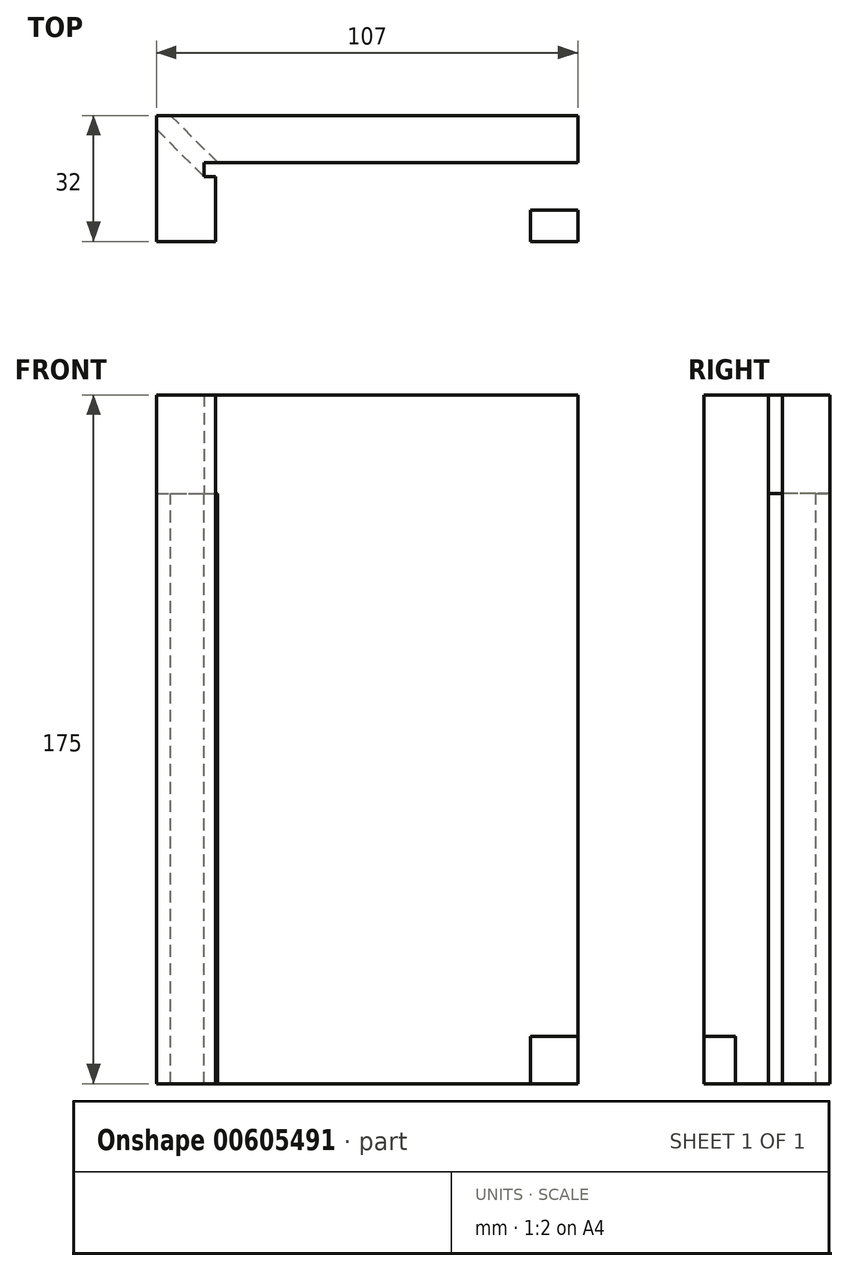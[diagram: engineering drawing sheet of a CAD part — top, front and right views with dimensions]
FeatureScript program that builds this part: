
annotation { "Feature Type Name" : "Feature", "Feature Type Description" : "" }
export const myFeature = defineFeature(function(context is Context, id is Id, definition is map)
    precondition{}
    {
        {
            var Q0;
            Q0=qCreatedBy(makeId("Top.planeOp"),FACE);
            var sketch = newSketch(context, id + "F0", { "sketchPlane" : qUnion([Q0])});
            skLineSegment(sketch, "E0", {"start": v(-28.32, 70.71) * mm, "end": v(-28.32, -10.33) * mm, "construction": true});
            skLineSegment(sketch, "E1", {"start": v(-27.64, -6.28) * mm, "end": v(-11.03, -22.9) * mm, "construction": true});
            skLineSegment(sketch, "E2", {"start": v(-15.41, -17.56) * mm, "end": v(106.8, -17.56) * mm, "construction": true});
            skLineSegment(sketch, "E3.0", {"start": v(-26.02, 70.71) * mm, "end": v(-26.02, -10.33) * mm, "construction": true});
            skLineSegment(sketch, "E4.0", {"start": v(-26.02, -4.66) * mm, "end": v(-9.4, -21.27) * mm, "construction": true});
            skLineSegment(sketch, "E5.0", {"start": v(-15.41, -15.26) * mm, "end": v(106.8, -15.26) * mm, "construction": true});
            skLineSegment(sketch, "E6.bottom", {"start": v(-15.41, -15.26) * mm, "end": v(79.59, -15.26) * mm});
            skLineSegment(sketch, "E6.top", {"start": v(-15.41, -3.26) * mm, "end": v(79.59, -3.26) * mm});
            skLineSegment(sketch, "E6.left", {"start": v(-15.41, -15.26) * mm, "end": v(-15.41, -3.26) * mm});
            skLineSegment(sketch, "E6.right", {"start": v(79.59, -15.26) * mm, "end": v(79.59, -3.26) * mm});
            skLineSegment(sketch, "E7.bottom", {"start": v(-15.41, -15.26) * mm, "end": v(-27.41, -15.26) * mm});
            skLineSegment(sketch, "E7.top", {"start": v(-15.41, -35.26) * mm, "end": v(-27.41, -35.26) * mm});
            skLineSegment(sketch, "E7.left", {"start": v(-15.41, -15.26) * mm, "end": v(-15.41, -35.26) * mm});
            skLineSegment(sketch, "E7.right", {"start": v(-27.41, -15.26) * mm, "end": v(-27.41, -35.26) * mm});
            skLineSegment(sketch, "E8.top", {"start": v(-15.41, -3.26) * mm, "end": v(-27.41, -3.26) * mm});
            skLineSegment(sketch, "E8.right", {"start": v(-27.41, -15.26) * mm, "end": v(-27.41, -3.26) * mm});
            skLineSegment(sketch, "E9", {"start": v(-27.41, -3.26) * mm, "end": v(-15.41, -15.26) * mm});
            skLineSegment(sketch, "E10.0", {"start": v(-27.79, -6.42) * mm, "end": v(-11.17, -23.04) * mm});
            skLineSegment(sketch, "E11.0", {"start": v(-23.88, -3.26) * mm, "end": v(-7.64, -19.5) * mm});
            skSolve(sketch);
        }
        {
            var Q0;
            {var subQ1=sQuery(id+"F0.wireOp",EDGE,"E6.top");Q0=makeQuery(id+"F0.imprint","IMPRINT",FACE,{"disambiguationData":[TD([[makeQuery(id+"F0.imprint","IMPRINT",EDGE,{"derivedFrom":subQ1}),-1.0]])]});}
            var Q1;
            {var subQ1=sQuery(id+"F0.wireOp",EDGE,"E8.top");var subQ3=sQuery(id+"F0.wireOp",EDGE,"E11.0");var subQ4=makeQuery(id+"F0.imprint","INTERSECT",VERTEX,{"derivedFrom":[subQ1,subQ3]});Q1=makeQuery(id+"F0.imprint","IMPRINT",FACE,{"disambiguationData":[TD([[makeQuery(id+"F0.imprint","IMPRINT",EDGE,{"disambiguationData":[TD([[subQ4,-1.0]])],"derivedFrom":subQ3}),1.0]])]});}
            var Q2;
            {var subQ0=sQuery(id+"F0.wireOp",EDGE,"E9");Q2=makeQuery(id+"F0.imprint","IMPRINT",FACE,{"disambiguationData":[TD([[makeQuery(id+"F0.imprint","IMPRINT",EDGE,{"derivedFrom":subQ0}),-1.0]])]});}
            var Q3;
            {var subQ0=sQuery(id+"F0.wireOp",EDGE,"E8.right");var subQ3=sQuery(id+"F0.wireOp",EDGE,"E10.0");var subQ5=makeQuery(id+"F0.imprint","INTERSECT",VERTEX,{"derivedFrom":[subQ0,subQ3]});Q3=makeQuery(id+"F0.imprint","IMPRINT",FACE,{"disambiguationData":[TD([[makeQuery(id+"F0.imprint","IMPRINT",EDGE,{"disambiguationData":[TD([[subQ5,-1.0]])],"derivedFrom":subQ3}),-1.0]])]});}
            var Q4;
            {var subQ6=sQuery(id+"F0.wireOp",EDGE,"E7.top");Q4=makeQuery(id+"F0.imprint","IMPRINT",FACE,{"disambiguationData":[TD([[makeQuery(id+"F0.imprint","IMPRINT",EDGE,{"derivedFrom":subQ6}),-1.0]])]});}
            var Q5;
            {var subQ0=sQuery(id+"F0.wireOp",EDGE,"E9");Q5=makeQuery(id+"F0.imprint","IMPRINT",FACE,{"disambiguationData":[TD([[makeQuery(id+"F0.imprint","IMPRINT",EDGE,{"derivedFrom":subQ0}),1.0]])]});}
            var Q6;
            {var subQ1=sQuery(id+"F0.wireOp",EDGE,"E6.bottom");var subQ3=sQuery(id+"F0.wireOp",EDGE,"E11.0");var subQ4=makeQuery(id+"F0.imprint","INTERSECT",VERTEX,{"derivedFrom":[subQ1,subQ3]});Q6=makeQuery(id+"F0.imprint","IMPRINT",FACE,{"disambiguationData":[TD([[makeQuery(id+"F0.imprint","IMPRINT",EDGE,{"disambiguationData":[TD([[subQ4,1.0]])],"derivedFrom":subQ3}),-1.0]])]});}
            var Q7;
            {var subQ1=sQuery(id+"F0.wireOp",EDGE,"E7.left");var subQ3=sQuery(id+"F0.wireOp",EDGE,"E10.0");var subQ4=makeQuery(id+"F0.imprint","INTERSECT",VERTEX,{"derivedFrom":[subQ1,subQ3]});Q7=makeQuery(id+"F0.imprint","IMPRINT",FACE,{"disambiguationData":[TD([[makeQuery(id+"F0.imprint","IMPRINT",EDGE,{"disambiguationData":[TD([[subQ4,1.0]])],"derivedFrom":subQ3}),1.0]])]});}
            extrude(context, id + "F1", {"entities" : qUnion([Q0, Q1, Q2, Q3, Q4, Q5, Q6, Q7]), "depth" : 25 * mm, "offsetDistance" : 25 * mm});
        }
        {
            var Q0;
            {var subQ6=sQuery(id+"F0.wireOp",EDGE,"E7.top");Q0=makeQuery(id+"F0.imprint","IMPRINT",FACE,{"disambiguationData":[TD([[makeQuery(id+"F0.imprint","IMPRINT",EDGE,{"derivedFrom":subQ6}),-1.0]])]});}
            var Q1;
            {var subQ1=sQuery(id+"F0.wireOp",EDGE,"E8.top");var subQ3=sQuery(id+"F0.wireOp",EDGE,"E11.0");var subQ4=makeQuery(id+"F0.imprint","INTERSECT",VERTEX,{"derivedFrom":[subQ1,subQ3]});Q1=makeQuery(id+"F0.imprint","IMPRINT",FACE,{"disambiguationData":[TD([[makeQuery(id+"F0.imprint","IMPRINT",EDGE,{"disambiguationData":[TD([[subQ4,-1.0]])],"derivedFrom":subQ3}),1.0]])]});}
            var Q2;
            {var subQ1=sQuery(id+"F0.wireOp",EDGE,"E6.top");Q2=makeQuery(id+"F0.imprint","IMPRINT",FACE,{"disambiguationData":[TD([[makeQuery(id+"F0.imprint","IMPRINT",EDGE,{"derivedFrom":subQ1}),-1.0]])]});}
            var Q3;
            {var subQ0=sQuery(id+"F0.wireOp",EDGE,"E8.right");var subQ3=sQuery(id+"F0.wireOp",EDGE,"E10.0");var subQ5=makeQuery(id+"F0.imprint","INTERSECT",VERTEX,{"derivedFrom":[subQ0,subQ3]});Q3=makeQuery(id+"F0.imprint","IMPRINT",FACE,{"disambiguationData":[TD([[makeQuery(id+"F0.imprint","IMPRINT",EDGE,{"disambiguationData":[TD([[subQ5,-1.0]])],"derivedFrom":subQ3}),-1.0]])]});}
            extrude(context, id + "F2", {"entities" : qUnion([Q0, Q1, Q2, Q3]), "operationType" : NewBodyOperationType.ADD, "oppositeDirection" : true, "depth" : 150 * mm, "offsetDistance" : 25 * mm});
        }
        {
            var Q0;
            Q0=makeQuery(id+"F2.opExtrude","CAP_FACE",FACE,{"disambiguationData":[OSD([sQuery(id+"F0.wireOp",EDGE,"E7.top"),sQuery(id+"F0.wireOp",EDGE,"E7.left"),sQuery(id+"F0.wireOp",EDGE,"E7.right"),sQuery(id+"F0.wireOp",EDGE,"E8.right"),sQuery(id+"F0.wireOp",EDGE,"E10.0")])],"isStart":false});
            var sketch = newSketch(context, id + "F3", { "sketchPlane" : qUnion([Q0])});
            skLineSegment(sketch, "E12.bottom", {"start": v(-15.41, 18.8) * mm, "end": v(-12.41, 18.8) * mm});
            skLineSegment(sketch, "E12.left", {"start": v(-15.41, 18.8) * mm, "end": v(-15.41, 30.8) * mm});
            skLineSegment(sketch, "E12.right", {"start": v(-12.41, 18.8) * mm, "end": v(-12.41, 30.8) * mm});
            skLineSegment(sketch, "E13.top", {"start": v(-12.41, 35.26) * mm, "end": v(-15.41, 35.26) * mm});
            skLineSegment(sketch, "E13.left", {"start": v(-12.41, 30.8) * mm, "end": v(-12.41, 35.26) * mm});
            skLineSegment(sketch, "E13.right", {"start": v(-15.41, 30.8) * mm, "end": v(-15.41, 35.26) * mm});
            skSolve(sketch);
        }
        {
            var Q0;
            Q0 = qSketchRegion(id + "F3", true);
            var Q1;
            Q1=makeQuery(id+"F1.opExtrude","CAP_FACE",FACE,{"disambiguationData":[OSD([sQuery(id+"F0.wireOp",EDGE,"E6.bottom"),sQuery(id+"F0.wireOp",EDGE,"E6.top"),sQuery(id+"F0.wireOp",EDGE,"E6.right"),sQuery(id+"F0.wireOp",EDGE,"E7.top"),sQuery(id+"F0.wireOp",EDGE,"E7.left"),sQuery(id+"F0.wireOp",EDGE,"E7.right"),sQuery(id+"F0.wireOp",EDGE,"E8.top"),sQuery(id+"F0.wireOp",EDGE,"E8.right")])],"isStart":false});
            extrude(context, id + "F4", {"entities" : qUnion([Q0]), "operationType" : NewBodyOperationType.ADD, "endBound" : BoundingType.UP_TO_SURFACE, "oppositeDirection" : true, "depth" : 25 * mm, "endBoundEntityFace" : qUnion([Q1]), "offsetDistance" : 25 * mm});
        }
        {
            var Q0;
            Q0=makeQuery(id+"F2.opExtrude","CAP_FACE",FACE,{"disambiguationData":[OSD([sQuery(id+"F0.wireOp",EDGE,"E6.bottom"),sQuery(id+"F0.wireOp",EDGE,"E6.top"),sQuery(id+"F0.wireOp",EDGE,"E6.right"),sQuery(id+"F0.wireOp",EDGE,"E8.top"),sQuery(id+"F0.wireOp",EDGE,"E11.0")])],"isStart":false});
            var sketch = newSketch(context, id + "F5", { "sketchPlane" : qUnion([Q0])});
            skLineSegment(sketch, "E14.0.0", {"start": v(-12.41, 30.8) * mm, "end": v(-12.41, 35.26) * mm});
            skLineSegment(sketch, "E14.0.1", {"start": v(-12.41, 35.26) * mm, "end": v(-15.41, 35.26) * mm});
            skLineSegment(sketch, "E14.0.2", {"start": v(-15.41, 35.26) * mm, "end": v(-15.41, 30.8) * mm});
            skLineSegment(sketch, "E14.0.3", {"start": v(-15.41, 30.8) * mm, "end": v(-15.41, 18.8) * mm});
            skLineSegment(sketch, "E14.0.4", {"start": v(-15.41, 18.8) * mm, "end": v(-12.41, 18.8) * mm});
            skLineSegment(sketch, "E14.0.5", {"start": v(-12.41, 18.8) * mm, "end": v(-12.41, 30.8) * mm});
            skLineSegment(sketch, "E15.bottom", {"start": v(79.59, 15.26) * mm, "end": v(-12.41, 15.26) * mm});
            skLineSegment(sketch, "E15.top", {"start": v(79.59, 35.26) * mm, "end": v(-12.41, 35.26) * mm});
            skLineSegment(sketch, "E15.left", {"start": v(79.59, 15.26) * mm, "end": v(79.59, 35.26) * mm});
            skLineSegment(sketch, "E15.right", {"start": v(-12.41, 15.26) * mm, "end": v(-12.41, 35.26) * mm});
            skLineSegment(sketch, "E16.top", {"start": v(79.59, 27.26) * mm, "end": v(-12.41, 27.26) * mm});
            skLineSegment(sketch, "E16.left", {"start": v(79.59, 15.26) * mm, "end": v(79.59, 27.26) * mm});
            skLineSegment(sketch, "E16.right", {"start": v(-12.41, 15.26) * mm, "end": v(-12.41, 27.26) * mm});
            skLineSegment(sketch, "E17.bottom", {"start": v(79.59, 35.26) * mm, "end": v(67.59, 35.26) * mm});
            skLineSegment(sketch, "E17.top", {"start": v(79.59, 15.26) * mm, "end": v(67.59, 15.26) * mm});
            skLineSegment(sketch, "E17.left", {"start": v(79.59, 35.26) * mm, "end": v(79.59, 15.26) * mm});
            skLineSegment(sketch, "E17.right", {"start": v(67.59, 35.26) * mm, "end": v(67.59, 15.26) * mm});
            skSolve(sketch);
        }
        {
            var Q0;
            {var subQ0=sQuery(id+"F5.wireOp",EDGE,"E15.top");Q0=makeQuery(id+"F5.imprint","IMPRINT",FACE,{"disambiguationData":[TD([[makeQuery(id+"F5.imprint","IMPRINT",EDGE,{"derivedFrom":subQ0}),1.0]])]});}
            var Q1;
            {var subQ5=sQuery(id+"F5.wireOp",EDGE,"E17.bottom");Q1=makeQuery(id+"F5.imprint","IMPRINT",FACE,{"disambiguationData":[TD([[makeQuery(id+"F5.imprint","IMPRINT",EDGE,{"derivedFrom":subQ5}),1.0]])]});}
            var Q2;
            {var subQ5=sQuery(id+"F5.wireOp",EDGE,"E17.top");Q2=makeQuery(id+"F5.imprint","IMPRINT",FACE,{"disambiguationData":[TD([[makeQuery(id+"F5.imprint","IMPRINT",EDGE,{"derivedFrom":subQ5}),1.0]])]});}
            extrude(context, id + "F6", {"entities" : qUnion([Q0, Q1, Q2]), "operationType" : NewBodyOperationType.ADD, "oppositeDirection" : true, "depth" : 12 * mm, "offsetDistance" : 25 * mm});
        }
    });
